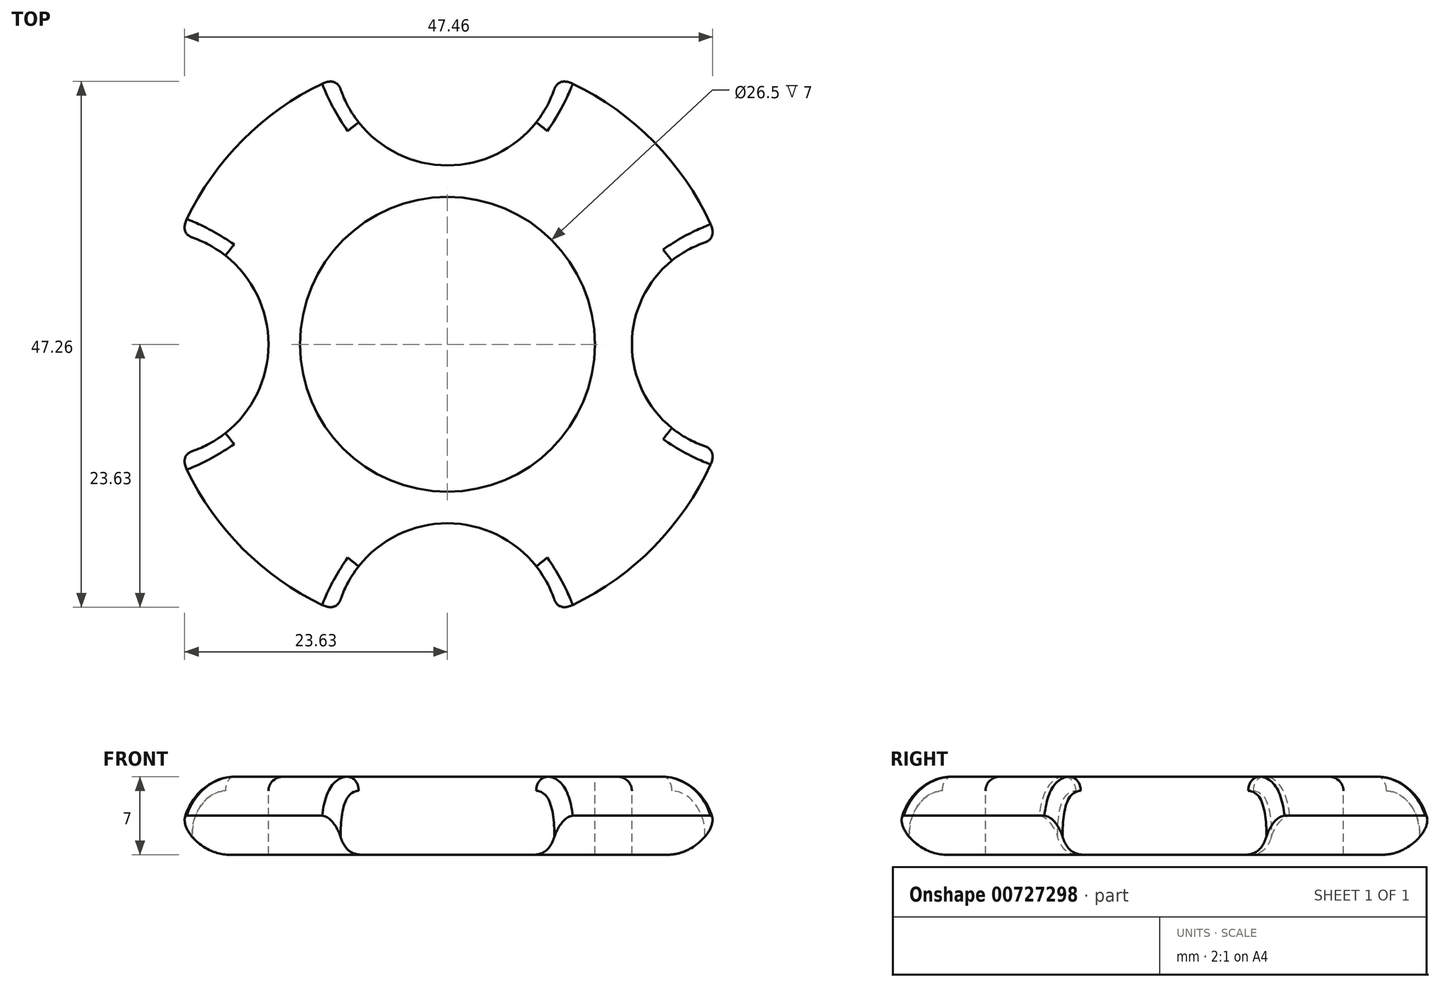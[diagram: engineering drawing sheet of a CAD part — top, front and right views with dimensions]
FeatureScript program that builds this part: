
annotation { "Feature Type Name" : "Feature", "Feature Type Description" : "" }
export const myFeature = defineFeature(function(context is Context, id is Id, definition is map)
    precondition{}
    {
        {
            var Q0;
            Q0=qCreatedBy(makeId("Top.planeOp"),FACE);
            var sketch = newSketch(context, id + "F0", { "sketchPlane" : qUnion([Q0])});
            skCircle(sketch, "E0", {"center": v(0, 0) * mm, "radius": 26.25 * mm});
            skSolve(sketch);
        }
        {
            var Q0;
            Q0=qSketchRegion(id+"F0",true);
            extrude(context, id + "F1", {"entities" : qUnion([Q0]), "depth" : 7 * mm, "offsetDistance" : 25.4 * mm});
        }
        {
            var Q0;
            Q0=makeQuery(id+"F1.opExtrude","CAP_FACE",FACE,{"disambiguationData":[OSD([sQuery(id+"F0.wireOp",EDGE,"E0")])],"isStart":false});
            var sketch = newSketch(context, id + "F2", { "sketchPlane" : qUnion([Q0])});
            skCircle(sketch, "E1", {"center": v(0, 0) * mm, "radius": 13.25 * mm});
            skSolve(sketch);
        }
        {
            var Q0;
            Q0=qSketchRegion(id+"F2",true);
            extrude(context, id + "F3", {"entities" : qUnion([Q0]), "operationType" : NewBodyOperationType.REMOVE, "oppositeDirection" : true, "depth" : 25.4 * mm, "offsetDistance" : 25.4 * mm});
        }
        {
            var Q0;
            Q0=makeQuery(id+"F1.opExtrude","CAP_FACE",FACE,{"disambiguationData":[OSD([sQuery(id+"F0.wireOp",EDGE,"E0")])],"isStart":false});
            var sketch = newSketch(context, id + "F4", { "sketchPlane" : qUnion([Q0])});
            skCircle(sketch, "E2", {"center": v(0, -26.25) * mm, "radius": 10.16 * mm});
            skCircle(sketch, "E3", {"center": v(-26.25, 0) * mm, "radius": 10.16 * mm});
            skCircle(sketch, "E4", {"center": v(0, 26.25) * mm, "radius": 10.16 * mm});
            skCircle(sketch, "E5", {"center": v(26.25, 0) * mm, "radius": 9.67 * mm});
            skSolve(sketch);
        }
        {
            var Q0;
            Q0=qSketchRegion(id+"F4",true);
            extrude(context, id + "F5", {"entities" : qUnion([Q0]), "operationType" : NewBodyOperationType.REMOVE, "oppositeDirection" : true, "depth" : 25.4 * mm, "offsetDistance" : 25.4 * mm});
        }
        {
            var Q0;
            {var subQ0=sQuery(id+"F0.wireOp",EDGE,"E0");Q0=makeQuery(id+"F5.boolean.opBoolean","SPLIT",EDGE,{"disambiguationData":[TD([makeQuery(id+"F1.opExtrude","SWEPT_FACE",FACE,{"disambiguationData":[OSD([subQ0])]}),makeQuery(id+"F1.opExtrude","CAP_FACE",FACE,{"disambiguationData":[OSD([subQ0])],"isStart":true}),makeQuery(id+"F5.opExtrude","SWEPT_FACE",FACE,{"disambiguationData":[OSD([sQuery(id+"F4.wireOp",EDGE,"E2")])]}),makeQuery(id+"F5.opExtrude","SWEPT_FACE",FACE,{"disambiguationData":[OSD([sQuery(id+"F4.wireOp",EDGE,"E5")])]})])],"derivedFrom":makeQuery(id+"F1.opExtrude","CAP_EDGE",EDGE,{"disambiguationData":[OSD([subQ0])],"isStart":true})});}
            var Q1;
            {var subQ0=sQuery(id+"F0.wireOp",EDGE,"E0");Q1=makeQuery(id+"F5.boolean.opBoolean","SPLIT",EDGE,{"disambiguationData":[TD([makeQuery(id+"F1.opExtrude","SWEPT_FACE",FACE,{"disambiguationData":[OSD([subQ0])]}),makeQuery(id+"F1.opExtrude","CAP_FACE",FACE,{"disambiguationData":[OSD([subQ0])],"isStart":true}),makeQuery(id+"F5.opExtrude","SWEPT_FACE",FACE,{"disambiguationData":[OSD([sQuery(id+"F4.wireOp",EDGE,"E2")])]}),makeQuery(id+"F5.opExtrude","SWEPT_FACE",FACE,{"disambiguationData":[OSD([sQuery(id+"F4.wireOp",EDGE,"E3")])]})])],"derivedFrom":makeQuery(id+"F1.opExtrude","CAP_EDGE",EDGE,{"disambiguationData":[OSD([subQ0])],"isStart":true})});}
            var Q2;
            {var subQ0=sQuery(id+"F0.wireOp",EDGE,"E0");Q2=makeQuery(id+"F5.boolean.opBoolean","SPLIT",EDGE,{"disambiguationData":[TD([makeQuery(id+"F1.opExtrude","SWEPT_FACE",FACE,{"disambiguationData":[OSD([subQ0])]}),makeQuery(id+"F1.opExtrude","CAP_FACE",FACE,{"disambiguationData":[OSD([subQ0])],"isStart":true}),makeQuery(id+"F5.opExtrude","SWEPT_FACE",FACE,{"disambiguationData":[OSD([sQuery(id+"F4.wireOp",EDGE,"E3")])]}),makeQuery(id+"F5.opExtrude","SWEPT_FACE",FACE,{"disambiguationData":[OSD([sQuery(id+"F4.wireOp",EDGE,"E4")])]})])],"derivedFrom":makeQuery(id+"F1.opExtrude","CAP_EDGE",EDGE,{"disambiguationData":[OSD([subQ0])],"isStart":true})});}
            var Q3;
            {var subQ0=sQuery(id+"F0.wireOp",EDGE,"E0");Q3=makeQuery(id+"F5.boolean.opBoolean","SPLIT",EDGE,{"disambiguationData":[TD([makeQuery(id+"F1.opExtrude","SWEPT_FACE",FACE,{"disambiguationData":[OSD([subQ0])]}),makeQuery(id+"F1.opExtrude","CAP_FACE",FACE,{"disambiguationData":[OSD([subQ0])],"isStart":false}),makeQuery(id+"F5.opExtrude","SWEPT_FACE",FACE,{"disambiguationData":[OSD([sQuery(id+"F4.wireOp",EDGE,"E3")])]}),makeQuery(id+"F5.opExtrude","SWEPT_FACE",FACE,{"disambiguationData":[OSD([sQuery(id+"F4.wireOp",EDGE,"E4")])]})])],"derivedFrom":makeQuery(id+"F1.opExtrude","CAP_EDGE",EDGE,{"disambiguationData":[OSD([subQ0])],"isStart":false})});}
            var Q4;
            {var subQ0=sQuery(id+"F0.wireOp",EDGE,"E0");Q4=makeQuery(id+"F5.boolean.opBoolean","SPLIT",EDGE,{"disambiguationData":[TD([makeQuery(id+"F1.opExtrude","SWEPT_FACE",FACE,{"disambiguationData":[OSD([subQ0])]}),makeQuery(id+"F1.opExtrude","CAP_FACE",FACE,{"disambiguationData":[OSD([subQ0])],"isStart":false}),makeQuery(id+"F5.opExtrude","SWEPT_FACE",FACE,{"disambiguationData":[OSD([sQuery(id+"F4.wireOp",EDGE,"E2")])]}),makeQuery(id+"F5.opExtrude","SWEPT_FACE",FACE,{"disambiguationData":[OSD([sQuery(id+"F4.wireOp",EDGE,"E3")])]})])],"derivedFrom":makeQuery(id+"F1.opExtrude","CAP_EDGE",EDGE,{"disambiguationData":[OSD([subQ0])],"isStart":false})});}
            var Q5;
            {var subQ0=sQuery(id+"F0.wireOp",EDGE,"E0");Q5=makeQuery(id+"F5.boolean.opBoolean","SPLIT",EDGE,{"disambiguationData":[TD([makeQuery(id+"F1.opExtrude","SWEPT_FACE",FACE,{"disambiguationData":[OSD([subQ0])]}),makeQuery(id+"F1.opExtrude","CAP_FACE",FACE,{"disambiguationData":[OSD([subQ0])],"isStart":false}),makeQuery(id+"F5.opExtrude","SWEPT_FACE",FACE,{"disambiguationData":[OSD([sQuery(id+"F4.wireOp",EDGE,"E2")])]}),makeQuery(id+"F5.opExtrude","SWEPT_FACE",FACE,{"disambiguationData":[OSD([sQuery(id+"F4.wireOp",EDGE,"E5")])]})])],"derivedFrom":makeQuery(id+"F1.opExtrude","CAP_EDGE",EDGE,{"disambiguationData":[OSD([subQ0])],"isStart":false})});}
            var Q6;
            {var subQ0=sQuery(id+"F0.wireOp",EDGE,"E0");Q6=makeQuery(id+"F5.boolean.opBoolean","SPLIT",EDGE,{"disambiguationData":[TD([makeQuery(id+"F1.opExtrude","SWEPT_FACE",FACE,{"disambiguationData":[OSD([subQ0])]}),makeQuery(id+"F1.opExtrude","CAP_FACE",FACE,{"disambiguationData":[OSD([subQ0])],"isStart":false}),makeQuery(id+"F5.opExtrude","SWEPT_FACE",FACE,{"disambiguationData":[OSD([sQuery(id+"F4.wireOp",EDGE,"E4")])]}),makeQuery(id+"F5.opExtrude","SWEPT_FACE",FACE,{"disambiguationData":[OSD([sQuery(id+"F4.wireOp",EDGE,"E5")])]})])],"derivedFrom":makeQuery(id+"F1.opExtrude","CAP_EDGE",EDGE,{"disambiguationData":[OSD([subQ0])],"isStart":false})});}
            var Q7;
            {var subQ0=sQuery(id+"F0.wireOp",EDGE,"E0");Q7=makeQuery(id+"F5.boolean.opBoolean","SPLIT",EDGE,{"disambiguationData":[TD([makeQuery(id+"F1.opExtrude","SWEPT_FACE",FACE,{"disambiguationData":[OSD([subQ0])]}),makeQuery(id+"F1.opExtrude","CAP_FACE",FACE,{"disambiguationData":[OSD([subQ0])],"isStart":true}),makeQuery(id+"F5.opExtrude","SWEPT_FACE",FACE,{"disambiguationData":[OSD([sQuery(id+"F4.wireOp",EDGE,"E4")])]}),makeQuery(id+"F5.opExtrude","SWEPT_FACE",FACE,{"disambiguationData":[OSD([sQuery(id+"F4.wireOp",EDGE,"E5")])]})])],"derivedFrom":makeQuery(id+"F1.opExtrude","CAP_EDGE",EDGE,{"disambiguationData":[OSD([subQ0])],"isStart":true})});}
            fillet(context, id + "F6", {"entities" : qUnion([Q0, Q1, Q2, Q3, Q4, Q5, Q6, Q7]), "radius" : 5.08 * mm, "tangentPropagation" : true, "allowEdgeOverflow" : false});
        }
        {
            var Q0;
            {var subQ0=makeQuery(id+"F5.opExtrude","SWEPT_FACE",FACE,{"disambiguationData":[OSD([sQuery(id+"F4.wireOp",EDGE,"E3")])]});var subQ1=sQuery(id+"F0.wireOp",EDGE,"E0");Q0=makeQuery(id+"F6.opFillet","BLEND_EDGE",EDGE,{"blendedFrom":[makeQuery(id+"F5.boolean.opBoolean","SPLIT",EDGE,{"disambiguationData":[TD([makeQuery(id+"F1.opExtrude","SWEPT_FACE",FACE,{"disambiguationData":[OSD([subQ1])]}),makeQuery(id+"F1.opExtrude","CAP_FACE",FACE,{"disambiguationData":[OSD([subQ1])],"isStart":false}),subQ0,makeQuery(id+"F5.opExtrude","SWEPT_FACE",FACE,{"disambiguationData":[OSD([sQuery(id+"F4.wireOp",EDGE,"E4")])]})])],"derivedFrom":makeQuery(id+"F1.opExtrude","CAP_EDGE",EDGE,{"disambiguationData":[OSD([subQ1])],"isStart":false})}),makeQuery(id+"F5.boolean.opBoolean","COPY",FACE,{"derivedFrom":subQ0})],"blendedInto":[makeQuery(id+"F5.boolean.opBoolean","COPY",FACE,{"derivedFrom":subQ0})]});}
            var Q1;
            {var subQ0=makeQuery(id+"F5.opExtrude","SWEPT_FACE",FACE,{"disambiguationData":[OSD([sQuery(id+"F4.wireOp",EDGE,"E4")])]});var subQ1=sQuery(id+"F0.wireOp",EDGE,"E0");Q1=makeQuery(id+"F6.opFillet","BLEND_EDGE",EDGE,{"blendedFrom":[makeQuery(id+"F5.boolean.opBoolean","SPLIT",EDGE,{"disambiguationData":[TD([makeQuery(id+"F1.opExtrude","SWEPT_FACE",FACE,{"disambiguationData":[OSD([subQ1])]}),makeQuery(id+"F1.opExtrude","CAP_FACE",FACE,{"disambiguationData":[OSD([subQ1])],"isStart":false}),makeQuery(id+"F5.opExtrude","SWEPT_FACE",FACE,{"disambiguationData":[OSD([sQuery(id+"F4.wireOp",EDGE,"E3")])]}),subQ0])],"derivedFrom":makeQuery(id+"F1.opExtrude","CAP_EDGE",EDGE,{"disambiguationData":[OSD([subQ1])],"isStart":false})}),makeQuery(id+"F5.boolean.opBoolean","COPY",FACE,{"derivedFrom":subQ0})],"blendedInto":[makeQuery(id+"F5.boolean.opBoolean","COPY",FACE,{"derivedFrom":subQ0})]});}
            var Q2;
            {var subQ0=makeQuery(id+"F5.opExtrude","SWEPT_FACE",FACE,{"disambiguationData":[OSD([sQuery(id+"F4.wireOp",EDGE,"E5")])]});var subQ1=sQuery(id+"F0.wireOp",EDGE,"E0");Q2=makeQuery(id+"F6.opFillet","BLEND_EDGE",EDGE,{"blendedFrom":[makeQuery(id+"F5.boolean.opBoolean","SPLIT",EDGE,{"disambiguationData":[TD([makeQuery(id+"F1.opExtrude","SWEPT_FACE",FACE,{"disambiguationData":[OSD([subQ1])]}),makeQuery(id+"F1.opExtrude","CAP_FACE",FACE,{"disambiguationData":[OSD([subQ1])],"isStart":false}),makeQuery(id+"F5.opExtrude","SWEPT_FACE",FACE,{"disambiguationData":[OSD([sQuery(id+"F4.wireOp",EDGE,"E4")])]}),subQ0])],"derivedFrom":makeQuery(id+"F1.opExtrude","CAP_EDGE",EDGE,{"disambiguationData":[OSD([subQ1])],"isStart":false})}),makeQuery(id+"F5.boolean.opBoolean","COPY",FACE,{"derivedFrom":subQ0})],"blendedInto":[makeQuery(id+"F5.boolean.opBoolean","COPY",FACE,{"derivedFrom":subQ0})]});}
            var Q3;
            {var subQ0=makeQuery(id+"F5.opExtrude","SWEPT_FACE",FACE,{"disambiguationData":[OSD([sQuery(id+"F4.wireOp",EDGE,"E2")])]});var subQ1=sQuery(id+"F0.wireOp",EDGE,"E0");Q3=makeQuery(id+"F6.opFillet","BLEND_EDGE",EDGE,{"blendedFrom":[makeQuery(id+"F5.boolean.opBoolean","SPLIT",EDGE,{"disambiguationData":[TD([makeQuery(id+"F1.opExtrude","SWEPT_FACE",FACE,{"disambiguationData":[OSD([subQ1])]}),makeQuery(id+"F1.opExtrude","CAP_FACE",FACE,{"disambiguationData":[OSD([subQ1])],"isStart":false}),subQ0,makeQuery(id+"F5.opExtrude","SWEPT_FACE",FACE,{"disambiguationData":[OSD([sQuery(id+"F4.wireOp",EDGE,"E5")])]})])],"derivedFrom":makeQuery(id+"F1.opExtrude","CAP_EDGE",EDGE,{"disambiguationData":[OSD([subQ1])],"isStart":false})}),makeQuery(id+"F5.boolean.opBoolean","COPY",FACE,{"derivedFrom":subQ0})],"blendedInto":[makeQuery(id+"F5.boolean.opBoolean","COPY",FACE,{"derivedFrom":subQ0})]});}
            fillet(context, id + "F7", {"entities" : qUnion([Q0, Q1, Q2, Q3]), "radius" : 1.27 * mm, "tangentPropagation" : true, "allowEdgeOverflow" : false});
        }
    });
